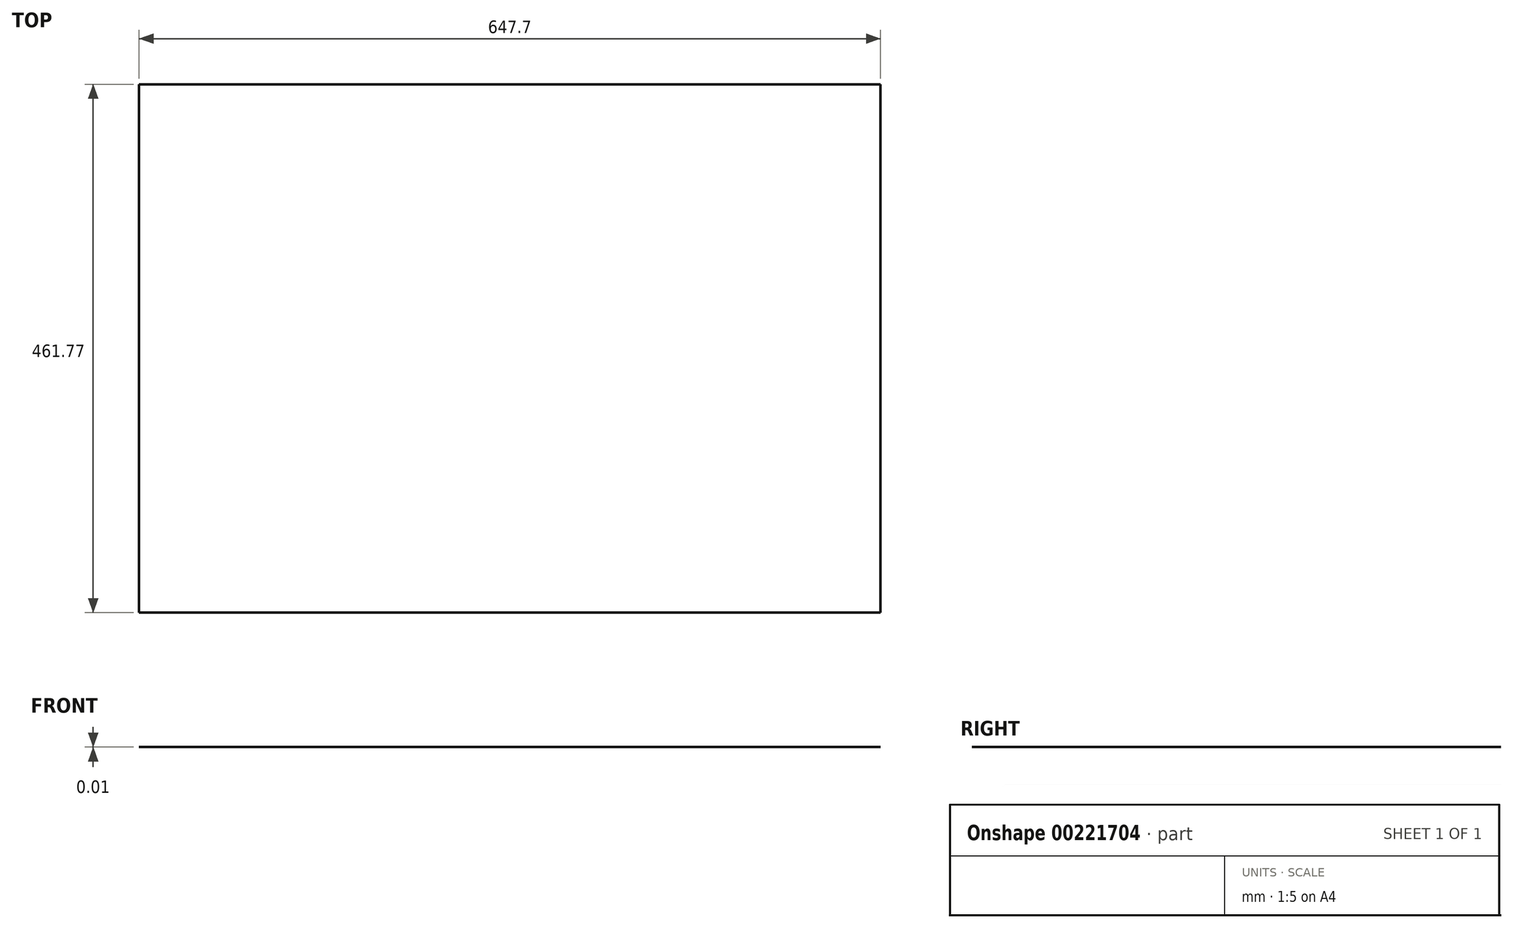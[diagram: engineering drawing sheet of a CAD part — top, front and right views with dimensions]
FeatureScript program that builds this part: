
annotation { "Feature Type Name" : "Feature", "Feature Type Description" : "" }
export const myFeature = defineFeature(function(context is Context, id is Id, definition is map)
    precondition{}
    {
        {
            var Q0;
            Q0=qCreatedBy(makeId("Top.planeOp"),FACE);
            var sketch = newSketch(context, id + "F0", { "sketchPlane" : qUnion([Q0])});
            skLineSegment(sketch, "E0.bottom", {"start": v(-343.58, -76.55) * mm, "end": v(304.12, -76.55) * mm});
            skLineSegment(sketch, "E0.top", {"start": v(-343.58, 385.22) * mm, "end": v(304.12, 385.22) * mm});
            skLineSegment(sketch, "E0.left", {"start": v(-343.58, -76.55) * mm, "end": v(-343.58, 385.22) * mm});
            skLineSegment(sketch, "E0.right", {"start": v(304.12, -76.55) * mm, "end": v(304.12, 385.22) * mm});
            skSolve(sketch);
        }
        {
            var Q0;
            Q0 = qSketchRegion(id + "F0", true);
            extrude(context, id + "F1", {"entities" : qUnion([Q0]), "oppositeDirection" : true, "depth" : 3 / 406.4 * mm});
        }
    });
